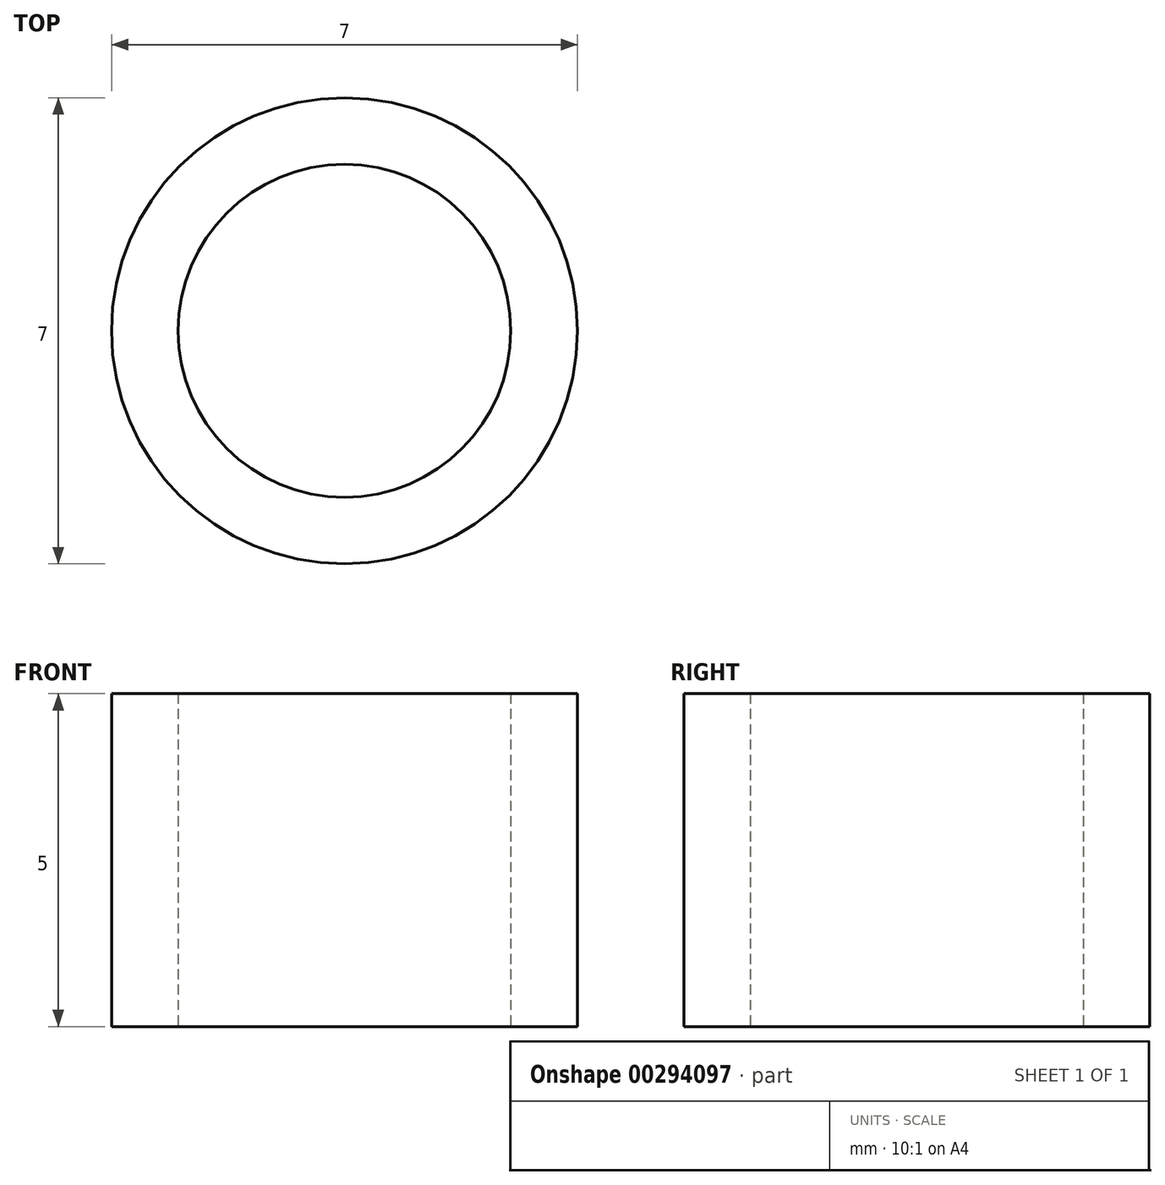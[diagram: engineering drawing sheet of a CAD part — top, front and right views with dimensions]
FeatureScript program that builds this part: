
annotation { "Feature Type Name" : "Feature", "Feature Type Description" : "" }
export const myFeature = defineFeature(function(context is Context, id is Id, definition is map)
    precondition{}
    {
        {
            var Q0;
            Q0=qCreatedBy(makeId("Top.planeOp"),FACE);
            var sketch = newSketch(context, id + "F0", { "sketchPlane" : qUnion([Q0])});
            skCircle(sketch, "E0", {"center": v(0, 0) * mm, "radius": 2.5 * mm});
            skCircle(sketch, "E1", {"center": v(0, 0) * mm, "radius": 3.5 * mm});
            skSolve(sketch);
        }
        {
            var Q0;
            Q0=makeQuery(id+"F0.imprint","IMPRINT",FACE,{"disambiguationData":[TD([[makeQuery(id+"F0.imprint","IMPRINT",EDGE,{"derivedFrom":sQuery(id+"F0.wireOp",EDGE,"E0")}),-1.0]])]});
            extrude(context, id + "F1", {"entities" : qUnion([Q0]), "depth" : 5 * mm});
        }
    });
